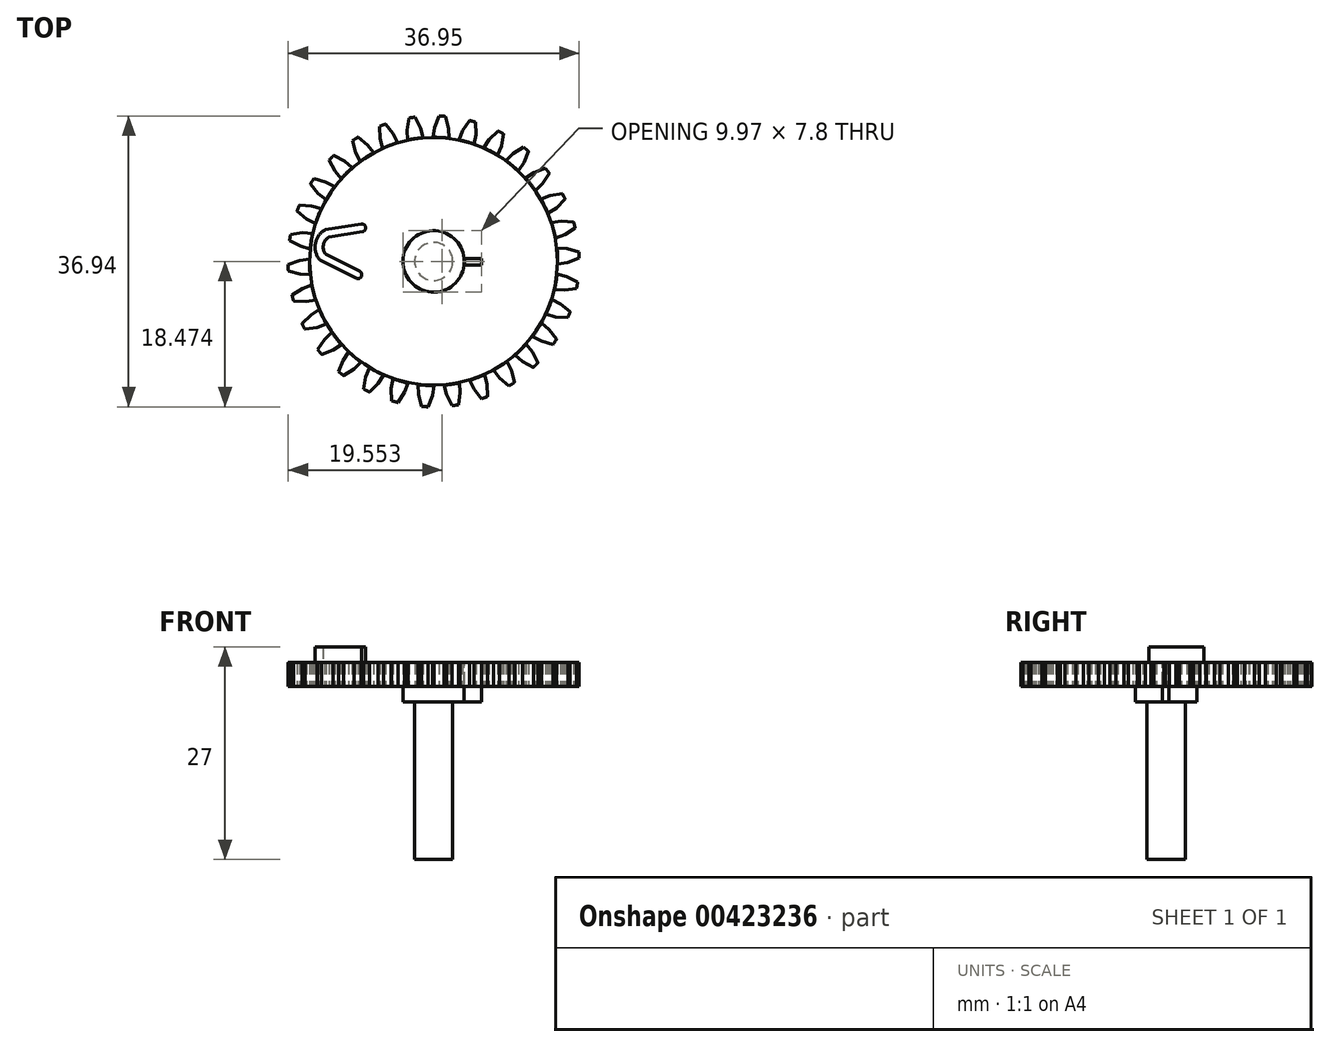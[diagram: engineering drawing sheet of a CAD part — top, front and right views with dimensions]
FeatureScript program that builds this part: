
annotation { "Feature Type Name" : "Feature", "Feature Type Description" : "" }
export const myFeature = defineFeature(function(context is Context, id is Id, definition is map)
    precondition{}
    {
        {
            var Q0;
            Q0=qCreatedBy(makeId("Top.planeOp"),FACE);
            var sketch = newSketch(context, id + "F0", { "sketchPlane" : qUnion([Q0])});
            skLineSegment(sketch, "E0", {"start": v(2.7, 43.64) * mm, "end": v(12.7, 43.64) * mm});
            skSolve(sketch);
        }
        {
            var Q0;
            Q0=qCreatedBy(makeId("Top.planeOp"),FACE);
            var sketch = newSketch(context, id + "F1", { "sketchPlane" : qUnion([Q0])});
            skLineSegment(sketch, "E1.0", {"start": v(2.7, 43.64) * mm, "end": v(12.7, 43.64) * mm});
            skLineSegment(sketch, "E2.top", {"start": v(2.7, -76.36) * mm, "end": v(12.7, -76.36) * mm});
            skLineSegment(sketch, "E2.left", {"start": v(2.7, 43.64) * mm, "end": v(2.7, -76.36) * mm});
            skLineSegment(sketch, "E2.right", {"start": v(12.7, 43.64) * mm, "end": v(12.7, -76.36) * mm});
            skLineSegment(sketch, "E3", {"start": v(2.7, 25.61) * mm, "end": v(12.7, 25.61) * mm, "construction": true});
            skLineSegment(sketch, "E4", {"start": v(-0.54, 23.36) * mm, "end": v(2.7, 23.36) * mm, "construction": true});
            skLineSegment(sketch, "E5.trimOffspring", {"start": v(12.7, 23.36) * mm, "end": v(15.96, 23.36) * mm, "construction": true});
            skSolve(sketch);
        }
        {
            var Q0;
            Q0=qCreatedBy(makeId("Top.planeOp"),FACE);
            var sketch = newSketch(context, id + "F2", { "sketchPlane" : qUnion([Q0])});
            skCircle(sketch, "E6", {"center": v(-27.08, -9.47) * mm, "radius": 3.83 * mm, "construction": true});
            skPoint(sketch, "E6.first.point", {"position": v(-30.8, -8.51) * mm});
            skPoint(sketch, "E6.second.point", {"position": v(-24.15, -7) * mm});
            skPoint(sketch, "E6.third.point", {"position": v(-26, -13.15) * mm});
            skPoint(sketch, "E7.0", {"position": v(7.7, 43.64) * mm});
            skLineSegment(sketch, "E8", {"start": v(7.7, -76.2) * mm, "end": v(7.7, 35.56) * mm, "construction": true});
            skLineSegment(sketch, "E9", {"start": v(85.63, -9.47) * mm, "end": v(-27.08, -9.47) * mm, "construction": true});
            skCircle(sketch, "E10.MirrorC", {"center": v(42.47, -9.47) * mm, "radius": 3.83 * mm, "construction": true});
            skCircle(sketch, "E11", {"center": v(-27.08, -9.47) * mm, "radius": 15.77 * mm, "construction": true});
            skCircle(sketch, "E12.MirrorC", {"center": v(42.47, -9.47) * mm, "radius": 15.77 * mm, "construction": true});
            skCircle(sketch, "E13.MirrorC", {"center": v(7.7, -9.47) * mm, "radius": 3.83 * mm, "construction": true});
            skCircle(sketch, "E14.MirrorC", {"center": v(7.7, -9.47) * mm, "radius": 15.77 * mm, "construction": true});
            skSolve(sketch);
        }
        {
            var Q0;
            Q0=qCreatedBy(makeId("Top.planeOp"),FACE);
            var sketch = newSketch(context, id + "F3", { "sketchPlane" : qUnion([Q0])});
            skPoint(sketch, "E15.0", {"position": v(42.47, -9.47) * mm});
            skCircle(sketch, "E16.0", {"center": v(42.47, -9.47) * mm, "radius": 15.77 * mm});
            skCircle(sketch, "E17.0", {"center": v(42.47, -9.47) * mm, "radius": 3.83 * mm});
            skLineSegment(sketch, "E18.0", {"start": v(7.7, -76.2) * mm, "end": v(7.7, 35.56) * mm});
            skLineSegment(sketch, "E19.0", {"start": v(85.63, -9.47) * mm, "end": v(-27.08, -9.47) * mm});
            skCircle(sketch, "E20.0", {"center": v(7.7, -9.47) * mm, "radius": 3.83 * mm});
            skCircle(sketch, "E21.0", {"center": v(-27.08, -9.47) * mm, "radius": 3.83 * mm});
            skCircle(sketch, "E22", {"center": v(42.47, -9.47) * mm, "radius": 15.73 * mm});
            skCircle(sketch, "E23", {"center": v(42.47, -9.47) * mm, "radius": 3.9 * mm});
            skArc(sketch, "E24", {"start": v(38.49, 5.79) * mm, "mid": v(40.14, 6.13) * mm, "end": v(41.82, 6.29) * mm});
            skLineSegment(sketch, "E25", {"start": v(39.15, 5.94) * mm, "end": v(39.08, 7.2) * mm});
            skLineSegment(sketch, "E26", {"start": v(42.47, -9.47) * mm, "end": v(40.14, 6.09) * mm, "construction": true});
            skPoint(sketch, "E26.endSnap0", {"position": v(40.14, 6.13) * mm});
            skLineSegment(sketch, "E27", {"start": v(40.14, 6.09) * mm, "end": v(39.58, 9.82) * mm, "construction": true});
            skLineSegment(sketch, "E28", {"start": v(39.08, 7.2) * mm, "end": v(39.33, 8.74) * mm});
            skLineSegment(sketch, "E29.MirrorCS", {"start": v(40.82, 7.46) * mm, "end": v(40.13, 8.86) * mm});
            skLineSegment(sketch, "E30.MirrorCS", {"start": v(41.13, 6.24) * mm, "end": v(40.82, 7.46) * mm});
            skArc(sketch, "E31.trimOffspring", {"start": v(40.13, 8.86) * mm, "mid": v(39.73, 8.8) * mm, "end": v(39.33, 8.74) * mm});
            skSolve(sketch);
        }
        {
            var Q0;
            {var subQ0=sQuery(id+"F3.wireOp",EDGE,"E22");var subQ1=sQuery(id+"F3.wireOp",EDGE,"E19.0");var subQ2=makeQuery(id+"F3.imprint","INTERSECT",VERTEX,{"disambiguationData":[OD(0.0)],"derivedFrom":[subQ1,subQ0]});Q0=makeQuery(id+"F3.imprint","IMPRINT",FACE,{"disambiguationData":[TD([[makeQuery(id+"F3.imprint","IMPRINT",EDGE,{"disambiguationData":[TD([[subQ2,-1.0]])],"derivedFrom":subQ1}),-1.0]])]});}
            var Q1;
            {var subQ0=sQuery(id+"F3.wireOp",EDGE,"E22");var subQ1=sQuery(id+"F3.wireOp",EDGE,"E19.0");var subQ2=makeQuery(id+"F3.imprint","INTERSECT",VERTEX,{"disambiguationData":[OD(0.0)],"derivedFrom":[subQ1,subQ0]});Q1=makeQuery(id+"F3.imprint","IMPRINT",FACE,{"disambiguationData":[TD([[makeQuery(id+"F3.imprint","IMPRINT",EDGE,{"disambiguationData":[TD([[subQ2,-1.0]])],"derivedFrom":subQ1}),1.0]])]});}
            extrude(context, id + "F4", {"entities" : qUnion([Q0, Q1]), "depth" : 3 * mm});
        }
        {
            var Q0;
            Q0=qSketchRegion(id+"F2",true);
            var Q1;
            {var subQ0=sQuery(id+"F3.wireOp",EDGE,"E25");Q1=makeQuery(id+"F3.imprint","IMPRINT",FACE,{"disambiguationData":[TD([[makeQuery(id+"F3.imprint","IMPRINT",EDGE,{"derivedFrom":subQ0}),-1.0]])]});}
            var Q2;
            Q2=makeQuery(id+"F4.opExtrude","CAP_FACE",FACE,{"disambiguationData":[OSD([sQuery(id+"F3.wireOp",EDGE,"E22"),sQuery(id+"F3.wireOp",EDGE,"E23")])],"isStart":false});
            extrude(context, id + "F5", {"entities" : qUnion([Q0, Q1]), "endBound" : BoundingType.UP_TO_SURFACE, "endBoundEntityFace" : qUnion([Q2]), "depth" : 25 * mm});
        }
        {
            var Q0;
            Q0=makeQuery(id+"F5.opExtrude","SWEPT_BODY",BODY,{"disambiguationData":[OSD([sQuery(id+"F3.wireOp",EDGE,"E16.0"),sQuery(id+"F3.wireOp",EDGE,"E25"),sQuery(id+"F3.wireOp",EDGE,"E28"),sQuery(id+"F3.wireOp",EDGE,"E29.MirrorCS"),sQuery(id+"F3.wireOp",EDGE,"E30.MirrorCS"),sQuery(id+"F3.wireOp",EDGE,"E31.trimOffspring")])]});
            var Q1;
            Q1=sQuery(id+"F3.wireOp",EDGE,"E22");
            circularPattern(context, id + "F6", {"entities" : qUnion([Q0]), "axis" : qUnion([Q1]), "angle" : 360 * degree, "instanceCount" : 30, "equalSpace" : true, "isCentered" : true});
        }
        {
            var Q0;
            Q0=qCreatedBy(makeId("Top.planeOp"),FACE);
            var sketch = newSketch(context, id + "F7", { "sketchPlane" : qUnion([Q0])});
            skLineSegment(sketch, "E32", {"start": v(33.27, -4.72) * mm, "end": v(28.74, -5.44) * mm});
            skArc(sketch, "E33", {"start": v(28.68, -5.46) * mm, "mid": v(27.46, -7.2) * mm, "end": v(28, -9.25) * mm});
            skLineSegment(sketch, "E34", {"start": v(28.05, -9.3) * mm, "end": v(32.63, -11.6) * mm});
            skArc(sketch, "E35.0", {"start": v(29.1, -6.41) * mm, "mid": v(28.48, -7.36) * mm, "end": v(28.7, -8.48) * mm});
            skLineSegment(sketch, "E36.0", {"start": v(28.77, -8.54) * mm, "end": v(33.08, -10.71) * mm});
            skArc(sketch, "E37.filletArc", {"start": v(28.7, -8.48) * mm, "mid": v(28.74, -8.51) * mm, "end": v(28.77, -8.54) * mm});
            skPoint(sketch, "E38.visualSharp", {"position": v(28.7, -5.45) * mm});
            skArc(sketch, "E38.filletArc", {"start": v(28.74, -5.44) * mm, "mid": v(28.7, -5.45) * mm, "end": v(28.68, -5.46) * mm});
            skPoint(sketch, "E39.visualSharp", {"position": v(28.02, -9.28) * mm});
            skArc(sketch, "E39.filletArc", {"start": v(28, -9.25) * mm, "mid": v(28.02, -9.27) * mm, "end": v(28.05, -9.3) * mm});
            skLineSegment(sketch, "E40.0", {"start": v(33.43, -5.7) * mm, "end": v(29.17, -6.39) * mm});
            skArc(sketch, "E41", {"start": v(33.43, -5.7) * mm, "mid": v(33.84, -5.13) * mm, "end": v(33.27, -4.72) * mm});
            skArc(sketch, "E42", {"start": v(32.63, -11.6) * mm, "mid": v(33.3, -11.38) * mm, "end": v(33.08, -10.71) * mm});
            skArc(sketch, "E43.filletArc", {"start": v(29.17, -6.39) * mm, "mid": v(29.13, -6.4) * mm, "end": v(29.1, -6.41) * mm});
            skPoint(sketch, "E44.0", {"position": v(7.7, -9.47) * mm});
            skPoint(sketch, "E45.0", {"position": v(42.47, -9.47) * mm});
            skSolve(sketch);
        }
        {
            var Q0;
            Q0 = qSketchRegion(id + "F7", true);
            extrude(context, id + "F8", {"entities" : qUnion([Q0]), "operationType" : NewBodyOperationType.ADD, "depth" : 5 * mm});
        }
        {
            var Q0;
            Q0=makeQuery(id+"F4.opExtrude","CAP_FACE",FACE,{"disambiguationData":[OSD([sQuery(id+"F3.wireOp",EDGE,"E22"),sQuery(id+"F3.wireOp",EDGE,"E23")])],"isStart":false});
            var sketch = newSketch(context, id + "F9", { "sketchPlane" : qUnion([Q0])});
            skLineSegment(sketch, "E46.bottom", {"start": v(46.35, -9.94) * mm, "end": v(48.54, -9.94) * mm});
            skLineSegment(sketch, "E46.top", {"start": v(46.35, -9.12) * mm, "end": v(48.54, -9.12) * mm});
            skLineSegment(sketch, "E46.left", {"start": v(46.35, -9.94) * mm, "end": v(46.35, -9.12) * mm});
            skLineSegment(sketch, "E46.right", {"start": v(48.54, -9.94) * mm, "end": v(48.54, -9.12) * mm});
            skSolve(sketch);
        }
        {
            var Q0;
            {var subQ0=sQuery(id+"F9.wireOp",EDGE,"E46.bottom");Q0=makeQuery(id+"F9.imprint","IMPRINT",FACE,{"disambiguationData":[TD([[makeQuery(id+"F9.imprint","IMPRINT",EDGE,{"derivedFrom":subQ0}),1.0]])]});}
            extrude(context, id + "F10", {"entities" : qUnion([Q0]), "operationType" : NewBodyOperationType.REMOVE, "oppositeDirection" : true, "depth" : 25 * mm});
        }
        {
            var Q0;
            Q0=makeQuery(id+"F4.opExtrude","CAP_FACE",FACE,{"disambiguationData":[OSD([sQuery(id+"F3.wireOp",EDGE,"E22"),sQuery(id+"F3.wireOp",EDGE,"E23")])],"isStart":false});
            var sketch = newSketch(context, id + "F11", { "sketchPlane" : qUnion([Q0])});
            skCircle(sketch, "E47", {"center": v(42.47, -9.47) * mm, "radius": 3.9 * mm});
            skLineSegment(sketch, "E48.bottom", {"start": v(46.35, -9.94) * mm, "end": v(48.54, -9.94) * mm});
            skLineSegment(sketch, "E48.top", {"start": v(46.35, -9.12) * mm, "end": v(48.54, -9.12) * mm});
            skLineSegment(sketch, "E48.left", {"start": v(46.35, -9.94) * mm, "end": v(46.35, -9.12) * mm});
            skLineSegment(sketch, "E48.right", {"start": v(48.54, -9.94) * mm, "end": v(48.54, -9.12) * mm});
            skSolve(sketch);
        }
        {
            var Q0;
            {var subQ0=sQuery(id+"F11.wireOp",EDGE,"E48.bottom");Q0=makeQuery(id+"F11.imprint","IMPRINT",FACE,{"disambiguationData":[TD([[makeQuery(id+"F11.imprint","IMPRINT",EDGE,{"derivedFrom":subQ0}),1.0]])]});}
            var Q1;
            {var subQ0=sQuery(id+"F11.wireOp",EDGE,"E48.left");Q1=makeQuery(id+"F11.imprint","IMPRINT",FACE,{"disambiguationData":[TD([[makeQuery(id+"F11.imprint","IMPRINT",EDGE,{"derivedFrom":subQ0}),1.0]])]});}
            var Q2;
            Q2 = qBodyType(qCreatedBy(id + "F11" ,EDGE), BodyType.WIRE);
            var Q3;
            Q3=sQuery(id+"F11.wireOp",EDGE,"E48.bottom");
            var Q4;
            Q4=makeQuery(id+"F4.opExtrude","CAP_FACE",FACE,{"disambiguationData":[OSD([sQuery(id+"F3.wireOp",EDGE,"E22"),sQuery(id+"F3.wireOp",EDGE,"E23")])],"isStart":true});
            extrude(context, id + "F12", {"entities" : qUnion([Q0, Q1]), "surfaceEntities" : qUnion([Q2, Q3]), "oppositeDirection" : true, "endBoundEntityFace" : qUnion([Q4]), "depth" : 5 * mm});
        }
        {
            var Q0;
            Q0=makeQuery(id+"F12.opExtrude","CAP_FACE",FACE,{"disambiguationData":[OSD([sQuery(id+"F11.wireOp",EDGE,"E47"),sQuery(id+"F11.wireOp",EDGE,"E48.top"),sQuery(id+"F11.wireOp",EDGE,"E48.left")])],"isStart":false});
            var sketch = newSketch(context, id + "F13", { "sketchPlane" : qUnion([Q0])});
            skCircle(sketch, "E49", {"center": v(42.47, 9.47) * mm, "radius": 2.43 * mm});
            skSolve(sketch);
        }
        {
            var Q0;
            Q0=makeQuery(id+"F13.imprint","IMPRINT",FACE,{"disambiguationData":[TD([[makeQuery(id+"F13.imprint","IMPRINT",EDGE,{"derivedFrom":sQuery(id+"F13.wireOp",EDGE,"E49")}),1.0]])]});
            extrude(context, id + "F14", {"entities" : qUnion([Q0]), "operationType" : NewBodyOperationType.ADD, "depth" : 20 * mm});
        }
    });
